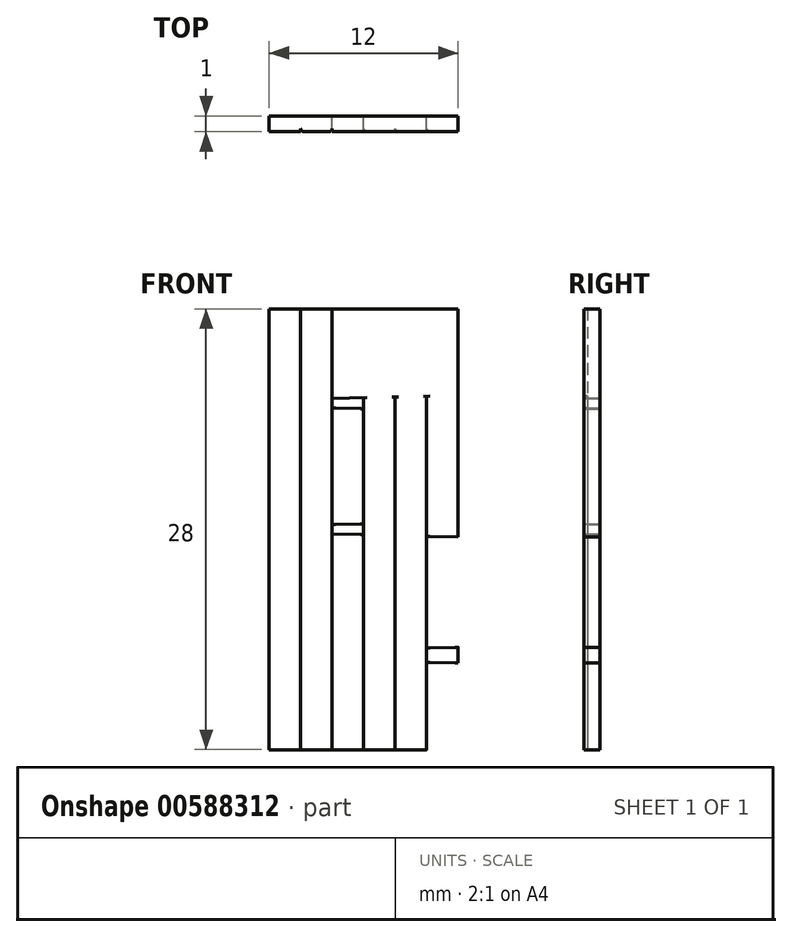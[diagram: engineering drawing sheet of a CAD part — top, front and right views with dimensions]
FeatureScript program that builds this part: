
annotation { "Feature Type Name" : "Feature", "Feature Type Description" : "" }
export const myFeature = defineFeature(function(context is Context, id is Id, definition is map)
    precondition{}
    {
        {
            var Q0;
            Q0=qCreatedBy(makeId("Front.planeOp"),FACE);
            var sketch = newSketch(context, id + "F0", { "sketchPlane" : qUnion([Q0])});
            skLineSegment(sketch, "E0.bottom", {"start": v(-103.32, -5.57) * mm, "end": v(-91.32, -5.57) * mm});
            skLineSegment(sketch, "E0.top", {"start": v(-103.32, -33.57) * mm, "end": v(-91.32, -33.57) * mm});
            skLineSegment(sketch, "E0.left", {"start": v(-103.32, -5.57) * mm, "end": v(-103.32, -33.57) * mm});
            skLineSegment(sketch, "E0.right", {"start": v(-91.32, -5.57) * mm, "end": v(-91.32, -15.07) * mm});
            skLineSegment(sketch, "E1", {"start": v(-91.32, -33.57) * mm, "end": v(-91.32, -28.07) * mm});
            skLineSegment(sketch, "E2", {"start": v(-99.32, -27.57) * mm, "end": v(-99.32, -27.27) * mm});
            skLineSegment(sketch, "E3", {"start": v(-91.32, -27.07) * mm, "end": v(-99.32, -27.27) * mm});
            skLineSegment(sketch, "E4", {"start": v(-91.32, -27.07) * mm, "end": v(-90.32, -27.07) * mm});
            skLineSegment(sketch, "E5", {"start": v(-90.32, -27.07) * mm, "end": v(-90.32, -27.57) * mm});
            skLineSegment(sketch, "E6.MirrorCS", {"start": v(-90.32, -28.07) * mm, "end": v(-90.32, -27.57) * mm});
            skLineSegment(sketch, "E7.MirrorCS", {"start": v(-91.32, -28.07) * mm, "end": v(-90.32, -28.07) * mm});
            skLineSegment(sketch, "E8.MirrorCS", {"start": v(-99.32, -27.57) * mm, "end": v(-99.32, -27.87) * mm});
            skLineSegment(sketch, "E9.MirrorCS", {"start": v(-91.32, -28.07) * mm, "end": v(-99.32, -27.87) * mm});
            skLineSegment(sketch, "E10.trimOffspring", {"start": v(-91.32, -28.07) * mm, "end": v(-91.32, -33.57) * mm});
            skLineSegment(sketch, "E11", {"start": v(-99.32, -15.57) * mm, "end": v(-99.32, -15.27) * mm});
            skLineSegment(sketch, "E12", {"start": v(-90.12, -15.57) * mm, "end": v(-90.12, -15.07) * mm});
            skLineSegment(sketch, "E13.MirrorCS", {"start": v(-90.12, -15.57) * mm, "end": v(-90.12, -16.07) * mm});
            skLineSegment(sketch, "E14.MirrorCS", {"start": v(-99.32, -15.57) * mm, "end": v(-99.32, -15.87) * mm});
            skLineSegment(sketch, "E15.trimOffspring", {"start": v(-91.32, -16.07) * mm, "end": v(-91.32, -27.07) * mm});
            skLineSegment(sketch, "E16", {"start": v(-103.32, -5.57) * mm, "end": v(-101.32, -5.57) * mm});
            skLineSegment(sketch, "E17", {"start": v(-101.32, -5.57) * mm, "end": v(-99.32, -5.57) * mm});
            skLineSegment(sketch, "E18", {"start": v(-99.32, -5.57) * mm, "end": v(-97.32, -5.57) * mm});
            skLineSegment(sketch, "E19", {"start": v(-97.32, -5.57) * mm, "end": v(-95.32, -5.57) * mm});
            skLineSegment(sketch, "E20", {"start": v(-95.32, -5.57) * mm, "end": v(-93.32, -5.57) * mm});
            skLineSegment(sketch, "E21", {"start": v(-101.32, -5.57) * mm, "end": v(-101.32, -33.57) * mm});
            skLineSegment(sketch, "E22", {"start": v(-99.32, -5.57) * mm, "end": v(-99.32, -15.27) * mm});
            skLineSegment(sketch, "E23", {"start": v(-97.32, -5.57) * mm, "end": v(-97.32, -33.57) * mm});
            skLineSegment(sketch, "E24", {"start": v(-95.32, -5.57) * mm, "end": v(-95.32, -33.57) * mm});
            skLineSegment(sketch, "E25", {"start": v(-93.32, -5.57) * mm, "end": v(-93.32, -33.57) * mm});
            skLineSegment(sketch, "E26", {"start": v(-91.32, -15.07) * mm, "end": v(-91.32, -16.07) * mm});
            skLineSegment(sketch, "E27", {"start": v(-91.32, -27.07) * mm, "end": v(-91.32, -28.07) * mm});
            skLineSegment(sketch, "E28.trimOffspring", {"start": v(-99.32, -15.57) * mm, "end": v(-99.32, -33.57) * mm});
            skLineSegment(sketch, "E29", {"start": v(-91.32, -5.57) * mm, "end": v(-91.32, -11.07) * mm});
            skLineSegment(sketch, "E30", {"start": v(-91.32, -11.07) * mm, "end": v(-90.32, -11.07) * mm});
            skLineSegment(sketch, "E31", {"start": v(-90.32, -11.07) * mm, "end": v(-90.32, -12.07) * mm});
            skLineSegment(sketch, "E32", {"start": v(-90.32, -12.07) * mm, "end": v(-91.32, -12.07) * mm});
            skLineSegment(sketch, "E33", {"start": v(-91.32, -11.07) * mm, "end": v(-91.32, -11.57) * mm});
            skLineSegment(sketch, "E34", {"start": v(-99.32, -11.57) * mm, "end": v(-99.32, -11.27) * mm});
            skLineSegment(sketch, "E35", {"start": v(-99.32, -11.27) * mm, "end": v(-91.32, -11.07) * mm});
            skLineSegment(sketch, "E36", {"start": v(-99.32, -11.57) * mm, "end": v(-99.32, -11.87) * mm});
            skLineSegment(sketch, "E37", {"start": v(-99.32, -11.87) * mm, "end": v(-91.32, -12.07) * mm});
            skLineSegment(sketch, "E38", {"start": v(-91.32, -12.07) * mm, "end": v(-91.32, -19.57) * mm});
            skLineSegment(sketch, "E39", {"start": v(-91.32, -19.57) * mm, "end": v(-91.32, -20.07) * mm});
            skLineSegment(sketch, "E40", {"start": v(-91.32, -20.07) * mm, "end": v(-90.32, -20.07) * mm});
            skLineSegment(sketch, "E41", {"start": v(-90.32, -20.07) * mm, "end": v(-90.32, -19.07) * mm});
            skLineSegment(sketch, "E42", {"start": v(-90.32, -19.07) * mm, "end": v(-91.32, -19.07) * mm});
            skLineSegment(sketch, "E43", {"start": v(-99.32, -19.57) * mm, "end": v(-99.32, -19.27) * mm});
            skLineSegment(sketch, "E44", {"start": v(-99.32, -19.27) * mm, "end": v(-91.32, -19.07) * mm});
            skLineSegment(sketch, "E45", {"start": v(-99.32, -19.57) * mm, "end": v(-99.32, -19.87) * mm});
            skLineSegment(sketch, "E46", {"start": v(-99.32, -19.87) * mm, "end": v(-91.32, -20.07) * mm});
            skSolve(sketch);
        }
        {
            var Q0;
            {var subQ0=sQuery(id+"F0.wireOp",EDGE,"E0.left");Q0=makeQuery(id+"F0.imprint","IMPRINT",FACE,{"disambiguationData":[TD([[makeQuery(id+"F0.imprint","IMPRINT",EDGE,{"derivedFrom":subQ0}),1.0]])]});}
            extrude(context, id + "F1", {"entities" : qUnion([Q0]), "depth" : 1 * mm, "offsetDistance" : 25 * mm});
        }
        {
            var Q0;
            Q0=makeQuery(id+"F1.opExtrude","CAP_EDGE",EDGE,{"disambiguationData":[OSD([sQuery(id+"F0.wireOp",EDGE,"E0.left")])],"isStart":false});
            var Q1;
            Q1=makeQuery(id+"F1.opExtrude","CAP_EDGE",EDGE,{"disambiguationData":[OSD([sQuery(id+"F0.wireOp",EDGE,"E21")])],"isStart":false});
            fillet(context, id + "F2", {"entities" : qUnion([Q0, Q1]), "radius" : .2 * mm, "tangentPropagation" : true, "allowEdgeOverflow" : false});
        }
        {
            var Q0;
            {var subQ3=sQuery(id+"F0.wireOp",EDGE,"E11");Q0=makeQuery(id+"F0.imprint","IMPRINT",FACE,{"disambiguationData":[TD([[makeQuery(id+"F0.imprint","IMPRINT",EDGE,{"derivedFrom":subQ3}),1.0]])]});}
            extrude(context, id + "F3", {"entities" : qUnion([Q0]), "operationType" : NewBodyOperationType.ADD, "depth" : 1 * mm, "offsetDistance" : 25 * mm});
        }
        {
            var Q0;
            Q0=makeQuery(id+"F3.opExtrude","CAP_EDGE",EDGE,{"disambiguationData":[OSD([sQuery(id+"F0.wireOp",EDGE,"E21")])],"isStart":false});
            var Q1;
            Q1=makeQuery(id+"F3.opExtrude","CAP_EDGE",EDGE,{"disambiguationData":[OSD([sQuery(id+"F0.wireOp",EDGE,"E11"),sQuery(id+"F0.wireOp",EDGE,"E22"),sQuery(id+"F0.wireOp",EDGE,"E28.trimOffspring"),sQuery(id+"F0.wireOp",EDGE,"E34"),sQuery(id+"F0.wireOp",EDGE,"E36"),sQuery(id+"F0.wireOp",EDGE,"E43"),sQuery(id+"F0.wireOp",EDGE,"E45")])],"isStart":false});
            fillet(context, id + "F4", {"entities" : qUnion([Q0, Q1]), "radius" : .2 * mm, "tangentPropagation" : true, "allowEdgeOverflow" : false});
        }
        {
            var Q0;
            {var subQ1=sQuery(id+"F0.wireOp",EDGE,"E11");Q0=makeQuery(id+"F0.imprint","IMPRINT",FACE,{"disambiguationData":[TD([[makeQuery(id+"F0.imprint","IMPRINT",EDGE,{"derivedFrom":subQ1}),-1.0]])]});}
            var Q1;
            {var subQ0=sQuery(id+"F0.wireOp",EDGE,"E18");Q1=makeQuery(id+"F0.imprint","IMPRINT",FACE,{"disambiguationData":[TD([[makeQuery(id+"F0.imprint","IMPRINT",EDGE,{"derivedFrom":subQ0}),-1.0]])]});}
            var Q2;
            {var subQ1=sQuery(id+"F0.wireOp",EDGE,"E34");Q2=makeQuery(id+"F0.imprint","IMPRINT",FACE,{"disambiguationData":[TD([[makeQuery(id+"F0.imprint","IMPRINT",EDGE,{"derivedFrom":subQ1}),-1.0]])]});}
            var Q3;
            {var subQ1=sQuery(id+"F0.wireOp",EDGE,"E43");Q3=makeQuery(id+"F0.imprint","IMPRINT",FACE,{"disambiguationData":[TD([[makeQuery(id+"F0.imprint","IMPRINT",EDGE,{"derivedFrom":subQ1}),-1.0]])]});}
            var Q4;
            {var subQ0=sQuery(id+"F0.wireOp",EDGE,"E28.trimOffspring");var subQ1=sQuery(id+"F0.wireOp",EDGE,"E3");var subQ2=makeQuery(id+"F0.imprint","INTERSECT",VERTEX,{"derivedFrom":[subQ1,subQ0]});Q4=makeQuery(id+"F0.imprint","IMPRINT",FACE,{"disambiguationData":[TD([[makeQuery(id+"F0.imprint","IMPRINT",EDGE,{"disambiguationData":[TD([[subQ2,1.0]])],"derivedFrom":subQ1}),-1.0]])]});}
            var Q5;
            {var subQ0=sQuery(id+"F0.wireOp",EDGE,"E23");var subQ1=sQuery(id+"F0.wireOp",EDGE,"E0.top");var subQ2=makeQuery(id+"F0.imprint","INTERSECT",VERTEX,{"derivedFrom":[subQ1,subQ0]});Q5=makeQuery(id+"F0.imprint","IMPRINT",FACE,{"disambiguationData":[TD([[makeQuery(id+"F0.imprint","IMPRINT",EDGE,{"disambiguationData":[TD([[subQ2,1.0]])],"derivedFrom":subQ1}),1.0]])]});}
            var Q6;
            {var subQ0=sQuery(id+"F0.wireOp",EDGE,"E28.trimOffspring");var subQ1=sQuery(id+"F0.wireOp",EDGE,"E3");var subQ2=makeQuery(id+"F0.imprint","INTERSECT",VERTEX,{"derivedFrom":[subQ1,subQ0]});Q6=makeQuery(id+"F0.imprint","IMPRINT",FACE,{"disambiguationData":[TD([[makeQuery(id+"F0.imprint","IMPRINT",EDGE,{"disambiguationData":[TD([[subQ2,1.0]])],"derivedFrom":subQ1}),1.0]])]});}
            extrude(context, id + "F5", {"entities" : qUnion([Q0, Q1, Q2, Q3, Q4, Q5, Q6]), "operationType" : NewBodyOperationType.ADD, "depth" : 1 * mm, "offsetDistance" : 25 * mm});
        }
        {
            var Q0;
            Q0=makeQuery(id+"F5.opExtrude","CAP_EDGE",EDGE,{"disambiguationData":[OSD([sQuery(id+"F0.wireOp",EDGE,"E11"),sQuery(id+"F0.wireOp",EDGE,"E22"),sQuery(id+"F0.wireOp",EDGE,"E28.trimOffspring"),sQuery(id+"F0.wireOp",EDGE,"E34"),sQuery(id+"F0.wireOp",EDGE,"E36"),sQuery(id+"F0.wireOp",EDGE,"E43"),sQuery(id+"F0.wireOp",EDGE,"E45")])],"isStart":false});
            var Q1;
            Q1=makeQuery(id+"F5.opExtrude","CAP_EDGE",EDGE,{"disambiguationData":[OSD([sQuery(id+"F0.wireOp",EDGE,"E23")])],"isStart":false});
            fillet(context, id + "F6", {"entities" : qUnion([Q0, Q1]), "radius" : .2 * mm, "tangentPropagation" : true, "allowEdgeOverflow" : false});
        }
        {
            var Q0;
            {var subQ0=sQuery(id+"F0.wireOp",EDGE,"E19");Q0=makeQuery(id+"F0.imprint","IMPRINT",FACE,{"disambiguationData":[TD([[makeQuery(id+"F0.imprint","IMPRINT",EDGE,{"derivedFrom":subQ0}),-1.0]])]});}
            var Q1;
            {var subQ0=sQuery(id+"F0.wireOp",EDGE,"E35");var subQ1=sQuery(id+"F0.wireOp",EDGE,"E23");var subQ2=makeQuery(id+"F0.imprint","INTERSECT",VERTEX,{"derivedFrom":[subQ1,subQ0]});Q1=makeQuery(id+"F0.imprint","IMPRINT",FACE,{"disambiguationData":[TD([[makeQuery(id+"F0.imprint","IMPRINT",EDGE,{"disambiguationData":[TD([[subQ2,-1.0]])],"derivedFrom":subQ1}),1.0]])]});}
            var Q2;
            {var subQ0=sQuery(id+"F0.wireOp",EDGE,"E37");var subQ1=sQuery(id+"F0.wireOp",EDGE,"E23");var subQ2=makeQuery(id+"F0.imprint","INTERSECT",VERTEX,{"derivedFrom":[subQ1,subQ0]});Q2=makeQuery(id+"F0.imprint","IMPRINT",FACE,{"disambiguationData":[TD([[makeQuery(id+"F0.imprint","IMPRINT",EDGE,{"disambiguationData":[TD([[subQ2,-1.0]])],"derivedFrom":subQ1}),1.0]])]});}
            var Q3;
            {var subQ0=sQuery(id+"F0.wireOp",EDGE,"E44");var subQ1=sQuery(id+"F0.wireOp",EDGE,"E23");var subQ2=makeQuery(id+"F0.imprint","INTERSECT",VERTEX,{"derivedFrom":[subQ1,subQ0]});Q3=makeQuery(id+"F0.imprint","IMPRINT",FACE,{"disambiguationData":[TD([[makeQuery(id+"F0.imprint","IMPRINT",EDGE,{"disambiguationData":[TD([[subQ2,-1.0]])],"derivedFrom":subQ1}),1.0]])]});}
            var Q4;
            {var subQ0=sQuery(id+"F0.wireOp",EDGE,"E24");var subQ1=sQuery(id+"F0.wireOp",EDGE,"E3");var subQ2=makeQuery(id+"F0.imprint","INTERSECT",VERTEX,{"derivedFrom":[subQ1,subQ0]});Q4=makeQuery(id+"F0.imprint","IMPRINT",FACE,{"disambiguationData":[TD([[makeQuery(id+"F0.imprint","IMPRINT",EDGE,{"disambiguationData":[TD([[subQ2,-1.0]])],"derivedFrom":subQ1}),-1.0]])]});}
            var Q5;
            {var subQ0=sQuery(id+"F0.wireOp",EDGE,"E23");var subQ1=sQuery(id+"F0.wireOp",EDGE,"E0.top");var subQ2=makeQuery(id+"F0.imprint","INTERSECT",VERTEX,{"derivedFrom":[subQ1,subQ0]});Q5=makeQuery(id+"F0.imprint","IMPRINT",FACE,{"disambiguationData":[TD([[makeQuery(id+"F0.imprint","IMPRINT",EDGE,{"disambiguationData":[TD([[subQ2,-1.0]])],"derivedFrom":subQ1}),1.0]])]});}
            var Q6;
            {var subQ0=sQuery(id+"F0.wireOp",EDGE,"E24");var subQ1=sQuery(id+"F0.wireOp",EDGE,"E3");var subQ2=makeQuery(id+"F0.imprint","INTERSECT",VERTEX,{"derivedFrom":[subQ1,subQ0]});Q6=makeQuery(id+"F0.imprint","IMPRINT",FACE,{"disambiguationData":[TD([[makeQuery(id+"F0.imprint","IMPRINT",EDGE,{"disambiguationData":[TD([[subQ2,-1.0]])],"derivedFrom":subQ1}),1.0]])]});}
            extrude(context, id + "F7", {"entities" : qUnion([Q0, Q1, Q2, Q3, Q4, Q5, Q6]), "operationType" : NewBodyOperationType.ADD, "depth" : 1 * mm, "offsetDistance" : 25 * mm});
        }
        {
            var Q0;
            Q0=makeQuery(id+"F7.opExtrude","CAP_EDGE",EDGE,{"disambiguationData":[OSD([sQuery(id+"F0.wireOp",EDGE,"E23")])],"isStart":false});
            var Q1;
            Q1=makeQuery(id+"F7.opExtrude","CAP_EDGE",EDGE,{"disambiguationData":[OSD([sQuery(id+"F0.wireOp",EDGE,"E24")])],"isStart":false});
            fillet(context, id + "F8", {"entities" : qUnion([Q0, Q1]), "radius" : .2 * mm, "tangentPropagation" : true, "allowEdgeOverflow" : false});
        }
        {
            var Q0;
            {var subQ0=sQuery(id+"F0.wireOp",EDGE,"E20");Q0=makeQuery(id+"F0.imprint","IMPRINT",FACE,{"disambiguationData":[TD([[makeQuery(id+"F0.imprint","IMPRINT",EDGE,{"derivedFrom":subQ0}),-1.0]])]});}
            var Q1;
            {var subQ0=sQuery(id+"F0.wireOp",EDGE,"E35");var subQ1=sQuery(id+"F0.wireOp",EDGE,"E24");var subQ2=makeQuery(id+"F0.imprint","INTERSECT",VERTEX,{"derivedFrom":[subQ1,subQ0]});Q1=makeQuery(id+"F0.imprint","IMPRINT",FACE,{"disambiguationData":[TD([[makeQuery(id+"F0.imprint","IMPRINT",EDGE,{"disambiguationData":[TD([[subQ2,-1.0]])],"derivedFrom":subQ1}),1.0]])]});}
            var Q2;
            {var subQ0=sQuery(id+"F0.wireOp",EDGE,"E37");var subQ1=sQuery(id+"F0.wireOp",EDGE,"E24");var subQ2=makeQuery(id+"F0.imprint","INTERSECT",VERTEX,{"derivedFrom":[subQ1,subQ0]});Q2=makeQuery(id+"F0.imprint","IMPRINT",FACE,{"disambiguationData":[TD([[makeQuery(id+"F0.imprint","IMPRINT",EDGE,{"disambiguationData":[TD([[subQ2,-1.0]])],"derivedFrom":subQ1}),1.0]])]});}
            var Q3;
            {var subQ0=sQuery(id+"F0.wireOp",EDGE,"E44");var subQ1=sQuery(id+"F0.wireOp",EDGE,"E24");var subQ2=makeQuery(id+"F0.imprint","INTERSECT",VERTEX,{"derivedFrom":[subQ1,subQ0]});Q3=makeQuery(id+"F0.imprint","IMPRINT",FACE,{"disambiguationData":[TD([[makeQuery(id+"F0.imprint","IMPRINT",EDGE,{"disambiguationData":[TD([[subQ2,-1.0]])],"derivedFrom":subQ1}),1.0]])]});}
            var Q4;
            {var subQ0=sQuery(id+"F0.wireOp",EDGE,"E25");var subQ1=sQuery(id+"F0.wireOp",EDGE,"E3");var subQ2=makeQuery(id+"F0.imprint","INTERSECT",VERTEX,{"derivedFrom":[subQ1,subQ0]});Q4=makeQuery(id+"F0.imprint","IMPRINT",FACE,{"disambiguationData":[TD([[makeQuery(id+"F0.imprint","IMPRINT",EDGE,{"disambiguationData":[TD([[subQ2,-1.0]])],"derivedFrom":subQ1}),-1.0]])]});}
            var Q5;
            {var subQ0=sQuery(id+"F0.wireOp",EDGE,"E25");var subQ1=sQuery(id+"F0.wireOp",EDGE,"E3");var subQ2=makeQuery(id+"F0.imprint","INTERSECT",VERTEX,{"derivedFrom":[subQ1,subQ0]});Q5=makeQuery(id+"F0.imprint","IMPRINT",FACE,{"disambiguationData":[TD([[makeQuery(id+"F0.imprint","IMPRINT",EDGE,{"disambiguationData":[TD([[subQ2,-1.0]])],"derivedFrom":subQ1}),1.0]])]});}
            var Q6;
            {var subQ0=sQuery(id+"F0.wireOp",EDGE,"E24");var subQ1=sQuery(id+"F0.wireOp",EDGE,"E0.top");var subQ2=makeQuery(id+"F0.imprint","INTERSECT",VERTEX,{"derivedFrom":[subQ1,subQ0]});Q6=makeQuery(id+"F0.imprint","IMPRINT",FACE,{"disambiguationData":[TD([[makeQuery(id+"F0.imprint","IMPRINT",EDGE,{"disambiguationData":[TD([[subQ2,-1.0]])],"derivedFrom":subQ1}),1.0]])]});}
            extrude(context, id + "F9", {"entities" : qUnion([Q0, Q1, Q2, Q3, Q4, Q5, Q6]), "operationType" : NewBodyOperationType.ADD, "depth" : 1 * mm, "offsetDistance" : 25 * mm});
        }
        {
            var Q0;
            Q0=makeQuery(id+"F9.opExtrude","CAP_EDGE",EDGE,{"disambiguationData":[OSD([sQuery(id+"F0.wireOp",EDGE,"E24")])],"isStart":false});
            var Q1;
            Q1=makeQuery(id+"F9.opExtrude","CAP_EDGE",EDGE,{"disambiguationData":[OSD([sQuery(id+"F0.wireOp",EDGE,"E25")])],"isStart":false});
            fillet(context, id + "F10", {"entities" : qUnion([Q0, Q1]), "radius" : .2 * mm, "tangentPropagation" : true, "allowEdgeOverflow" : false});
        }
        {
            var Q0;
            {var subQ0=sQuery(id+"F0.wireOp",EDGE,"E0.bottom");Q0=makeQuery(id+"F0.imprint","IMPRINT",FACE,{"disambiguationData":[TD([[makeQuery(id+"F0.imprint","IMPRINT",EDGE,{"derivedFrom":subQ0}),-1.0]])]});}
            var Q1;
            {var subQ6=sQuery(id+"F0.wireOp",EDGE,"E0.right");Q1=makeQuery(id+"F0.imprint","IMPRINT",FACE,{"disambiguationData":[TD([[makeQuery(id+"F0.imprint","IMPRINT",EDGE,{"derivedFrom":subQ6}),-1.0]])]});}
            var Q2;
            {var subQ0=sQuery(id+"F0.wireOp",EDGE,"E37");var subQ1=sQuery(id+"F0.wireOp",EDGE,"E25");var subQ2=makeQuery(id+"F0.imprint","INTERSECT",VERTEX,{"derivedFrom":[subQ1,subQ0]});Q2=makeQuery(id+"F0.imprint","IMPRINT",FACE,{"disambiguationData":[TD([[makeQuery(id+"F0.imprint","IMPRINT",EDGE,{"disambiguationData":[TD([[subQ2,-1.0]])],"derivedFrom":subQ1}),1.0]])]});}
            var Q3;
            {var subQ0=sQuery(id+"F0.wireOp",EDGE,"E39");Q3=makeQuery(id+"F0.imprint","IMPRINT",FACE,{"disambiguationData":[TD([[makeQuery(id+"F0.imprint","IMPRINT",EDGE,{"derivedFrom":subQ0}),-1.0]])]});}
            var Q4;
            {var subQ0=sQuery(id+"F0.wireOp",EDGE,"E15.trimOffspring");Q4=makeQuery(id+"F0.imprint","IMPRINT",FACE,{"disambiguationData":[TD([[makeQuery(id+"F0.imprint","IMPRINT",EDGE,{"derivedFrom":subQ0}),-1.0]])]});}
            var Q5;
            {var subQ0=sQuery(id+"F0.wireOp",EDGE,"E27");Q5=makeQuery(id+"F0.imprint","IMPRINT",FACE,{"disambiguationData":[TD([[makeQuery(id+"F0.imprint","IMPRINT",EDGE,{"derivedFrom":subQ0}),-1.0]])]});}
            var Q6;
            {var subQ0=sQuery(id+"F0.wireOp",EDGE,"E10.trimOffspring");Q6=makeQuery(id+"F0.imprint","IMPRINT",FACE,{"disambiguationData":[TD([[makeQuery(id+"F0.imprint","IMPRINT",EDGE,{"derivedFrom":subQ0}),-1.0]])]});}
            extrude(context, id + "F11", {"entities" : qUnion([Q0, Q1, Q2, Q3, Q4, Q5, Q6]), "operationType" : NewBodyOperationType.ADD, "depth" : 1 * mm, "offsetDistance" : 25 * mm});
        }
        {
            var Q0;
            Q0=makeQuery(id+"F11.opExtrude","CAP_EDGE",EDGE,{"disambiguationData":[OSD([sQuery(id+"F0.wireOp",EDGE,"E25")])],"isStart":false});
            var Q1;
            Q1=makeQuery(id+"F11.opExtrude","CAP_EDGE",EDGE,{"disambiguationData":[OSD([sQuery(id+"F0.wireOp",EDGE,"E0.right"),sQuery(id+"F0.wireOp",EDGE,"E10.trimOffspring"),sQuery(id+"F0.wireOp",EDGE,"E15.trimOffspring"),sQuery(id+"F0.wireOp",EDGE,"E27"),sQuery(id+"F0.wireOp",EDGE,"E29"),sQuery(id+"F0.wireOp",EDGE,"E33"),sQuery(id+"F0.wireOp",EDGE,"E38"),sQuery(id+"F0.wireOp",EDGE,"E39")])],"isStart":false});
            fillet(context, id + "F12", {"entities" : qUnion([Q0, Q1]), "radius" : .2 * mm, "tangentPropagation" : true, "allowEdgeOverflow" : false});
        }
    });
